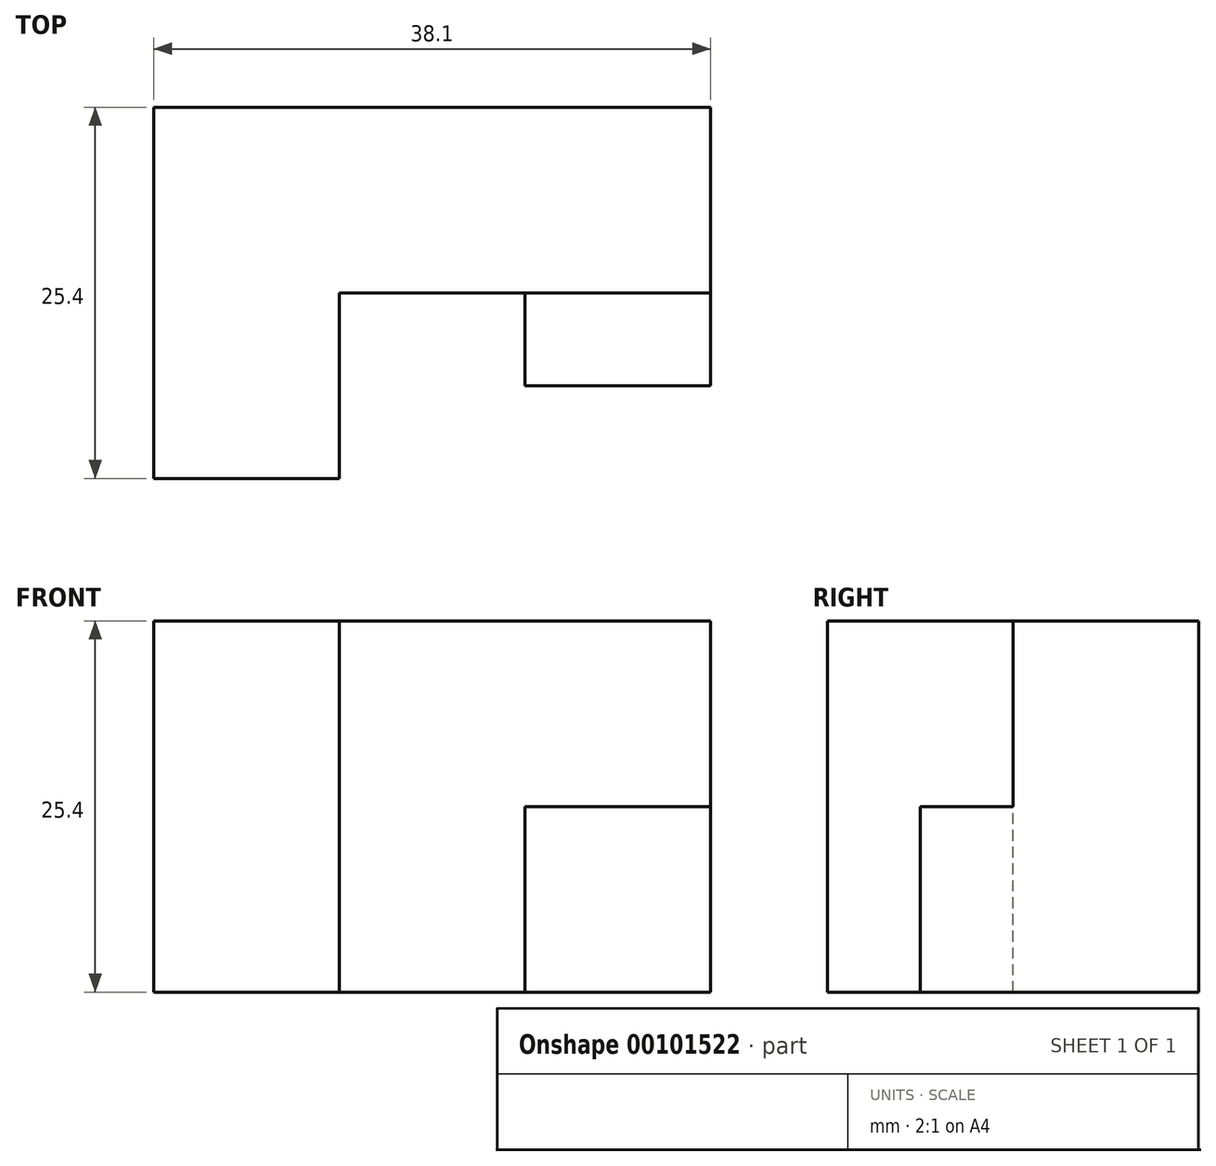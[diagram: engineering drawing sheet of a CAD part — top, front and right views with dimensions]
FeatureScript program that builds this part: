
annotation { "Feature Type Name" : "Feature", "Feature Type Description" : "" }
export const myFeature = defineFeature(function(context is Context, id is Id, definition is map)
    precondition{}
    {
        {
            var Q0;
            Q0=qCreatedBy(makeId("Top.planeOp"),FACE);
            var sketch = newSketch(context, id + "F0", { "sketchPlane" : qUnion([Q0])});
            skLineSegment(sketch, "E0.bottom", {"start": v(0, 0) * mm, "end": v(38.1, 0) * mm});
            skLineSegment(sketch, "E0.top", {"start": v(0, -25.4) * mm, "end": v(38.1, -25.4) * mm});
            skLineSegment(sketch, "E0.left", {"start": v(0, 0) * mm, "end": v(0, -25.4) * mm});
            skLineSegment(sketch, "E0.right", {"start": v(38.1, 0) * mm, "end": v(38.1, -25.4) * mm});
            skSolve(sketch);
        }
        {
            var Q0;
            Q0 = qSketchRegion(id + "F0", true);
            extrude(context, id + "F1", {"entities" : qUnion([Q0]), "depth" : 25.4 * mm});
        }
        {
            var Q0;
            Q0=qCreatedBy(makeId("Top.planeOp"),FACE);
            var sketch = newSketch(context, id + "F2", { "sketchPlane" : qUnion([Q0])});
            skLineSegment(sketch, "E1.bottom", {"start": v(0, 0) * mm, "end": v(12.7, 0) * mm});
            skLineSegment(sketch, "E1.top", {"start": v(0, -12.7) * mm, "end": v(12.7, -12.7) * mm});
            skLineSegment(sketch, "E1.left", {"start": v(0, 0) * mm, "end": v(0, -12.7) * mm});
            skLineSegment(sketch, "E1.right", {"start": v(12.7, 0) * mm, "end": v(12.7, -12.7) * mm});
            skLineSegment(sketch, "E2.bottom", {"start": v(12.7, -12.7) * mm, "end": v(38.1, -12.7) * mm});
            skLineSegment(sketch, "E2.top", {"start": v(12.7, -25.4) * mm, "end": v(38.1, -25.4) * mm});
            skLineSegment(sketch, "E2.left", {"start": v(12.7, -12.7) * mm, "end": v(12.7, -25.4) * mm});
            skLineSegment(sketch, "E2.right", {"start": v(38.1, -12.7) * mm, "end": v(38.1, -25.4) * mm});
            skLineSegment(sketch, "E3.bottom", {"start": v(12.7, -12.7) * mm, "end": v(27.35, -12.7) * mm});
            skLineSegment(sketch, "E3.top", {"start": v(12.7, -25.4) * mm, "end": v(27.35, -25.4) * mm});
            skLineSegment(sketch, "E3.right", {"start": v(27.35, -12.7) * mm, "end": v(27.35, -25.4) * mm});
            skSolve(sketch);
        }
        {
            var Q0;
            Q0=makeQuery(id+"F2.imprint","IMPRINT",FACE,{"disambiguationData":[TD([[makeQuery(id+"F2.imprint","IMPRINT",EDGE,{"derivedFrom":sQuery(id+"F2.wireOp",EDGE,"E2.bottom")}),-1.0]])]});
            var Q1;
            Q1=makeQuery(id+"F2.imprint","IMPRINT",FACE,{"disambiguationData":[TD([[makeQuery(id+"F2.imprint","IMPRINT",EDGE,{"derivedFrom":sQuery(id+"F2.wireOp",EDGE,"E3.top")}),1.0]])]});
            extrude(context, id + "F3", {"entities" : qUnion([Q0, Q1]), "operationType" : NewBodyOperationType.REMOVE, "endBound" : BoundingType.THROUGH_ALL, "depth" : 25.4 * mm});
        }
        {
            var Q0;
            Q0=qCreatedBy(makeId("Front.planeOp"),FACE);
            var sketch = newSketch(context, id + "F4", { "sketchPlane" : qUnion([Q0])});
            skLineSegment(sketch, "E4.bottom", {"start": v(0, 0) * mm, "end": v(25.4, 0) * mm});
            skLineSegment(sketch, "E4.top", {"start": v(0, 12.7) * mm, "end": v(25.4, 12.7) * mm});
            skLineSegment(sketch, "E4.left", {"start": v(0, 0) * mm, "end": v(0, 12.7) * mm});
            skLineSegment(sketch, "E4.right", {"start": v(25.4, 0) * mm, "end": v(25.4, 12.7) * mm});
            skLineSegment(sketch, "E5.bottom", {"start": v(25.4, 12.7) * mm, "end": v(38.1, 12.7) * mm});
            skLineSegment(sketch, "E5.top", {"start": v(25.4, 0) * mm, "end": v(38.1, 0) * mm});
            skLineSegment(sketch, "E5.left", {"start": v(25.4, 12.7) * mm, "end": v(25.4, 0) * mm});
            skLineSegment(sketch, "E5.right", {"start": v(38.1, 12.7) * mm, "end": v(38.1, 0) * mm});
            skSolve(sketch);
        }
        {
            var Q0;
            Q0=makeQuery(id+"F4.imprint","IMPRINT",FACE,{"disambiguationData":[TD([[makeQuery(id+"F4.imprint","IMPRINT",EDGE,{"derivedFrom":sQuery(id+"F4.wireOp",EDGE,"E5.bottom")}),-1.0]])]});
            extrude(context, id + "F5", {"entities" : qUnion([Q0]), "operationType" : NewBodyOperationType.ADD, "depth" : 19.05 * mm});
        }
    });
